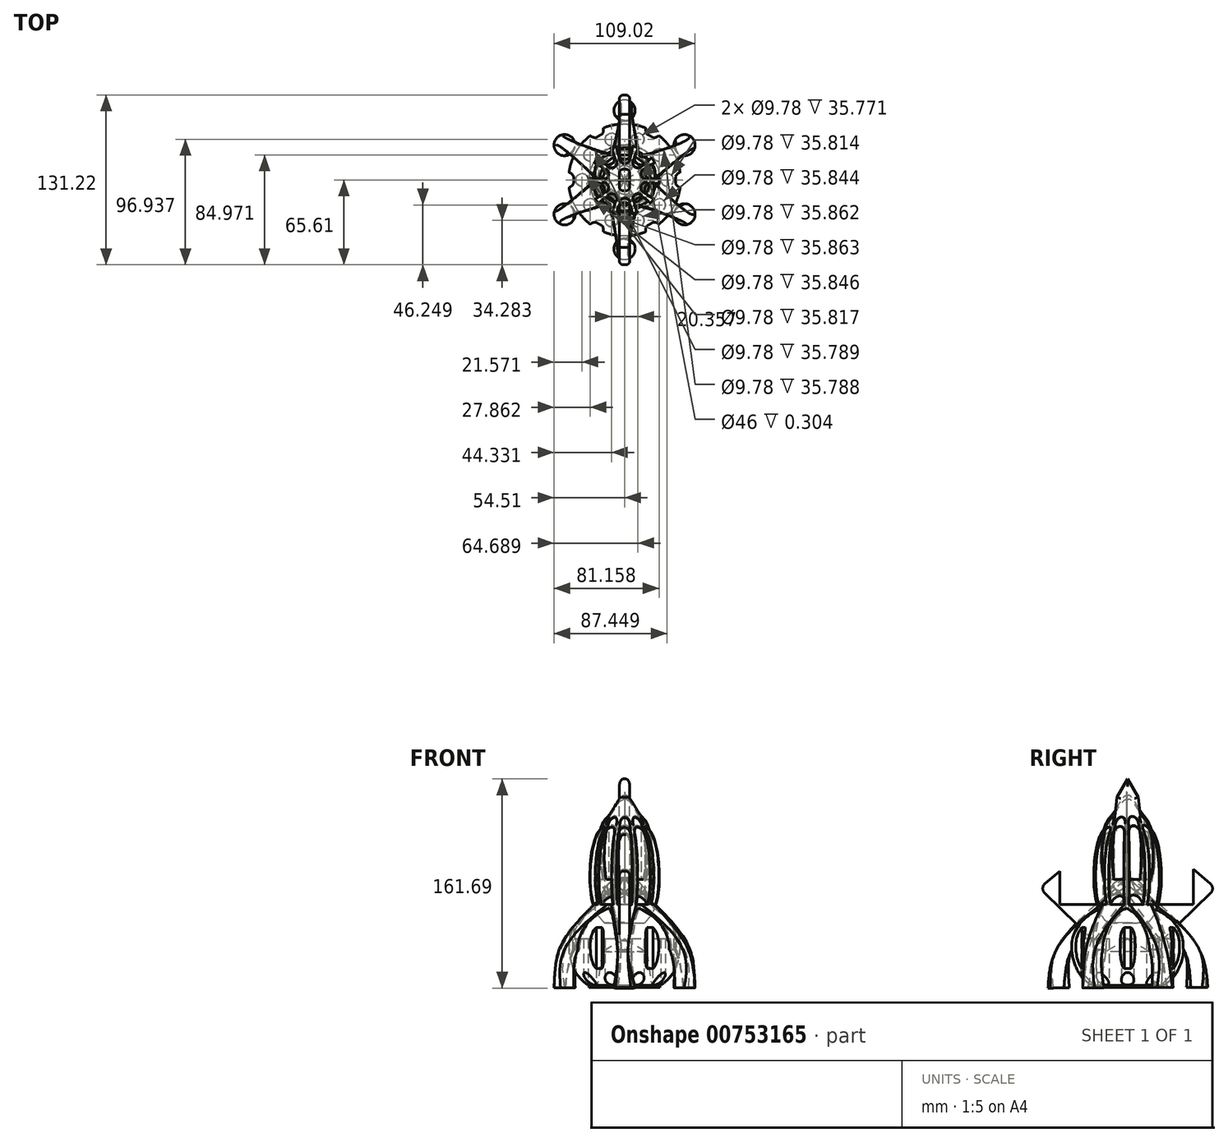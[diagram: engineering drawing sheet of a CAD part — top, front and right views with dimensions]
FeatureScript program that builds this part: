
annotation { "Feature Type Name" : "Feature", "Feature Type Description" : "" }
export const myFeature = defineFeature(function(context is Context, id is Id, definition is map)
    precondition{}
    {
        {
            var Q0;
            Q0=qCreatedBy(makeId("Top.planeOp"),FACE);
            cPlane(context, id + "F0", {"entities" : qUnion([Q0]), "cplaneType" : CPlaneType.OFFSET, "offset" : 28 * mm, "width" : 150 * mm, "height" : 150 * mm});
        }
        {
            var Q0;
            Q0=qCreatedBy(makeId("Top.planeOp"),FACE);
            var sketch = newSketch(context, id + "F1", { "sketchPlane" : qUnion([Q0])});
            skCircle(sketch, "E0", {"center": v(0, -53.65) * mm, "radius": 8.2 * mm});
            skCircle(sketch, "E1.1.0", {"center": v(46.46, -26.82) * mm, "radius": 8.2 * mm});
            skCircle(sketch, "E1.2.0", {"center": v(46.46, 26.82) * mm, "radius": 8.2 * mm});
            skCircle(sketch, "E1.4.0", {"center": v(-46.46, 26.82) * mm, "radius": 8.2 * mm});
            skPoint(sketch, "E1.center", {"position": v(0, 0) * mm});
            skCircle(sketch, "E2.1.5.0", {"center": v(-46.46, -26.82) * mm, "radius": 8.2 * mm});
            skArc(sketch, "E3", {"start": v(7.17, 57.63) * mm, "mid": v(1.7, 61.67) * mm, "end": v(-4.94, 60.2) * mm});
            skArc(sketch, "E4", {"start": v(6.58, 48.75) * mm, "mid": v(8.18, 53.1) * mm, "end": v(7.17, 57.63) * mm});
            skArc(sketch, "E5", {"start": v(-7.1, 49.56) * mm, "mid": v(-0.48, 45.47) * mm, "end": v(6.58, 48.75) * mm});
            skArc(sketch, "E6", {"start": v(-4.94, 60.2) * mm, "mid": v(-8.03, 55.29) * mm, "end": v(-7.1, 49.56) * mm});
            skSolve(sketch);
        }
        {
            var Q0;
            Q0=qCreatedBy(makeId("Right.planeOp"),FACE);
            var sketch = newSketch(context, id + "F2", { "sketchPlane" : qUnion([Q0])});
            skFitSpline(sketch, "E7", {"points": [v(53.84, 0) * mm, v(45.06, 43.34) * mm, v(0, 67.01) * mm], "startDerivative": vector(-1.6, 100.47) * mm, "endDerivative": vector(-104.87, 34.33) * mm});
            skSolve(sketch);
        }
        {
            var Q0;
            Q0=qCreatedBy(id+"F0.planeOp",FACE);
            var sketch = newSketch(context, id + "F3", { "sketchPlane" : qUnion([Q0])});
            skLineSegment(sketch, "E8.bottom", {"start": v(-2.65, 55.9) * mm, "end": v(5.35, 55.9) * mm});
            skLineSegment(sketch, "E8.top", {"start": v(-2.65, 43.9) * mm, "end": v(5.35, 43.9) * mm});
            skLineSegment(sketch, "E8.left", {"start": v(-2.65, 55.9) * mm, "end": v(-2.65, 43.9) * mm});
            skLineSegment(sketch, "E8.right", {"start": v(5.35, 55.9) * mm, "end": v(5.35, 43.9) * mm});
            skLineSegment(sketch, "E9.1.0", {"start": v(-55.65, 13.56) * mm, "end": v(-53.18, 21.17) * mm});
            skLineSegment(sketch, "E9.1.1", {"start": v(-44.24, 9.85) * mm, "end": v(-41.77, 17.46) * mm});
            skLineSegment(sketch, "E9.1.2", {"start": v(-55.65, 13.56) * mm, "end": v(-44.24, 9.85) * mm});
            skLineSegment(sketch, "E9.1.3", {"start": v(-53.18, 21.17) * mm, "end": v(-41.77, 17.46) * mm});
            skLineSegment(sketch, "E9.2.0", {"start": v(-31.77, -49.94) * mm, "end": v(-38.24, -45.23) * mm});
            skLineSegment(sketch, "E9.2.1", {"start": v(-24.71, -40.23) * mm, "end": v(-31.19, -35.53) * mm});
            skLineSegment(sketch, "E9.2.2", {"start": v(-31.77, -49.94) * mm, "end": v(-24.71, -40.23) * mm});
            skLineSegment(sketch, "E9.2.3", {"start": v(-38.24, -45.23) * mm, "end": v(-31.19, -35.53) * mm});
            skLineSegment(sketch, "E9.3.0", {"start": v(36, -46.84) * mm, "end": v(29.53, -51.54) * mm});
            skLineSegment(sketch, "E9.3.1", {"start": v(28.95, -37.13) * mm, "end": v(22.48, -41.83) * mm});
            skLineSegment(sketch, "E9.3.2", {"start": v(36, -46.84) * mm, "end": v(28.95, -37.13) * mm});
            skLineSegment(sketch, "E9.3.3", {"start": v(29.53, -51.54) * mm, "end": v(22.48, -41.83) * mm});
            skLineSegment(sketch, "E9.4.0", {"start": v(54, 18.57) * mm, "end": v(56.47, 10.96) * mm});
            skLineSegment(sketch, "E9.4.1", {"start": v(42.58, 14.86) * mm, "end": v(45.06, 7.25) * mm});
            skLineSegment(sketch, "E9.4.2", {"start": v(54, 18.57) * mm, "end": v(42.58, 14.86) * mm});
            skLineSegment(sketch, "E9.4.3", {"start": v(56.47, 10.96) * mm, "end": v(45.06, 7.25) * mm});
            skPoint(sketch, "E9.center", {"position": v(-0.02, -1.75) * mm});
            skSolve(sketch);
        }
        {
            var Q0;
            Q0=qCreatedBy(makeId("Right.planeOp"),FACE);
            var sketch = newSketch(context, id + "F4", { "sketchPlane" : qUnion([Q0])});
            skLineSegment(sketch, "E10", {"start": v(0.18, 0) * mm, "end": v(-21.05, 0) * mm});
            skFitSpline(sketch, "E11", {"points": [v(-21.05, 0) * mm, v(-42.02, 40.3) * mm, v(-8.37, 66.57) * mm, v(-0.13, 65.47) * mm], "startDerivative": vector(-109.76, 0) * mm, "endDerivative": vector(42.44, -18.45) * mm});
            skLineSegment(sketch, "E12", {"start": v(-0.13, 65.47) * mm, "end": v(0.18, 0) * mm});
            skLineSegment(sketch, "E13", {"start": v(-21.05, 0) * mm, "end": v(-17.07, 27.44) * mm});
            skLineSegment(sketch, "E14", {"start": v(-17.07, 27.44) * mm, "end": v(0, 37.41) * mm});
            skSolve(sketch);
        }
        {
            var Q0;
            {var subQ0=sQuery(id+"F4.wireOp",EDGE,"E11");Q0=makeQuery(id+"F4.imprint","IMPRINT",FACE,{"disambiguationData":[TD([[makeQuery(id+"F4.imprint","IMPRINT",EDGE,{"derivedFrom":subQ0}),-1.0]])]});}
            var Q1;
            Q1=sQuery(id+"F4.wireOp",EDGE,"E12");
            revolve(context, id + "F5", {"surfaceOperationType" : NewSurfaceOperationType.NEW, "entities" : qUnion([Q0]), "axis" : qUnion([Q1]), "revolveType" : RevolveType.FULL});
        }
        {
            var Q0;
            Q0=qCreatedBy(id+"F0.planeOp",FACE);
            cPlane(context, id + "F6", {"entities" : qUnion([Q0]), "cplaneType" : CPlaneType.OFFSET, "offset" : 36 * mm, "width" : 150 * mm, "height" : 150 * mm});
        }
        {
            var Q0;
            Q0=qCreatedBy(makeId("Front.planeOp"),FACE);
            var sketch = newSketch(context, id + "F7", { "sketchPlane" : qUnion([Q0])});
            skArc(sketch, "E15", {"start": v(-13.56, 78.8) * mm, "mid": v(-18.17, 66.48) * mm, "end": v(-13.26, 54.27) * mm});
            skArc(sketch, "E16", {"start": v(-13.26, 54.27) * mm, "mid": v(2.4, 48.69) * mm, "end": v(16.05, 58.17) * mm});
            skArc(sketch, "E17", {"start": v(16.05, 58.17) * mm, "mid": v(18.07, 68.66) * mm, "end": v(13.85, 78.48) * mm});
            skArc(sketch, "E18", {"start": v(13.85, 78.48) * mm, "mid": v(0.22, 84.88) * mm, "end": v(-13.56, 78.8) * mm});
            skSolve(sketch);
        }
        {
            var Q1;
            Q1=makeQuery(id+"F1.imprint","IMPRINT",FACE,{"disambiguationData":[TD([[makeQuery(id+"F1.imprint","IMPRINT",EDGE,{"derivedFrom":sQuery(id+"F1.wireOp",EDGE,"E3")}),1.0]])]});
            var Q2;
            Q2=makeQuery(id+"F3.imprint","IMPRINT",FACE,{"disambiguationData":[TD([[makeQuery(id+"F3.imprint","IMPRINT",EDGE,{"derivedFrom":sQuery(id+"F3.wireOp",EDGE,"E8.bottom")}),-1.0]])]});
            var Q3;
            Q3=makeQuery(id+"F7.imprint","IMPRINT",FACE,{"disambiguationData":[TD([[makeQuery(id+"F7.imprint","IMPRINT",EDGE,{"derivedFrom":sQuery(id+"F7.wireOp",EDGE,"E15")}),1.0]])]});
            var Q4;
            Q4=sQuery(id+"F2.wireOp",EDGE,"E7");
            loft(context, id + "F8", {"sheetProfilesArray" : [{ "sheetProfileEntities" : qUnion([Q1]) }, { "sheetProfileEntities" : qUnion([Q2]) }, { "sheetProfileEntities" : qUnion([Q3]) }], "guidesArray" : [{ "guideEntities" : qUnion([Q4]), "guideDerivativeType" : LoftGuideDerivativeType.DEFAULT, "guideDerivativeMagnitude" : 1 }]});
        }
        {
            var Q0;
            Q0=makeQuery(id+"F8.opLoft","SWEPT_BODY",BODY,{"disambiguationData":[OSD([makeQuery(id+"F1.imprint","IMPRINT",FACE,{"disambiguationData":[TD([[makeQuery(id+"F1.imprint","IMPRINT",EDGE,{"derivedFrom":sQuery(id+"F1.wireOp",EDGE,"E3")}),1.0]])]}),sQuery(id+"F3.wireOp",EDGE,"E8.left"),makeQuery(id+"F7.imprint","IMPRINT",FACE,{"disambiguationData":[TD([[makeQuery(id+"F7.imprint","IMPRINT",EDGE,{"derivedFrom":sQuery(id+"F7.wireOp",EDGE,"E15")}),1.0]])]})])]});
            var Q1;
            Q1=sQuery(id+"F4.wireOp",EDGE,"E12");
            circularPattern(context, id + "F9", {"operationType" : NewBodyOperationType.ADD, "entities" : qUnion([Q0]), "axis" : qUnion([Q1]), "angle" : 360 * degree, "instanceCount" : 6, "equalSpace" : true, "isCentered" : true});
        }
        {
            var Q0;
            Q0=qCreatedBy(makeId("Front.planeOp"),FACE);
            var sketch = newSketch(context, id + "F10", { "sketchPlane" : qUnion([Q0])});
            skFitSpline(sketch, "E19", {"points": [v(-15.35, 49.67) * mm, v(-24.47, 64.82) * mm, v(-25.38, 104.6) * mm, v(-19.75, 121) * mm, v(-12.6, 129.8) * mm, v(0, 145.27) * mm, v(10.93, 128.5) * mm], "startDerivative": vector(-59.94, 59.18) * mm, "endDerivative": vector(86, -27.64) * mm});
            skLineSegment(sketch, "E20", {"start": v(0, 50.04) * mm, "end": v(-15.35, 49.67) * mm});
            skLineSegment(sketch, "E21", {"start": v(0, 50.04) * mm, "end": v(0, 145.27) * mm});
            skSolve(sketch);
        }
        {
            var Q0;
            {var subQ0=sQuery(id+"F10.wireOp",EDGE,"E20");Q0=makeQuery(id+"F10.imprint","IMPRINT",FACE,{"disambiguationData":[TD([[makeQuery(id+"F10.imprint","IMPRINT",EDGE,{"derivedFrom":subQ0}),-1.0]])]});}
            var Q1;
            Q1=sQuery(id+"F10.wireOp",EDGE,"E21");
            revolve(context, id + "F11", {"surfaceOperationType" : NewSurfaceOperationType.NEW, "entities" : qUnion([Q0]), "axis" : qUnion([Q1]), "revolveType" : RevolveType.FULL});
        }
        {
            var Q0;
            {var subQ0=sQuery(id+"F10.wireOp",EDGE,"E20");Q0=makeQuery(id+"F10.imprint","IMPRINT",FACE,{"disambiguationData":[TD([[makeQuery(id+"F10.imprint","IMPRINT",EDGE,{"derivedFrom":subQ0}),-1.0]])]});}
            var Q1;
            Q1=sQuery(id+"F10.wireOp",EDGE,"E21");
            revolve(context, id + "F12", {"surfaceOperationType" : NewSurfaceOperationType.NEW, "entities" : qUnion([Q0]), "axis" : qUnion([Q1]), "revolveType" : RevolveType.FULL});
        }
        {
            var Q0;
            Q0=qCreatedBy(makeId("Right.planeOp"),FACE);
            var sketch = newSketch(context, id + "F13", { "sketchPlane" : qUnion([Q0])});
            skLineSegment(sketch, "E22", {"start": v(26.03, 35.86) * mm, "end": v(64.1, 72.83) * mm});
            skLineSegment(sketch, "E23", {"start": v(63.8, 80.26) * mm, "end": v(22.57, 114.6) * mm});
            skLineSegment(sketch, "E24", {"start": v(22.57, 114.6) * mm, "end": v(11.06, 122.62) * mm});
            skLineSegment(sketch, "E25", {"start": v(11.06, 122.62) * mm, "end": v(8.34, 146.93) * mm});
            skLineSegment(sketch, "E26", {"start": v(8.34, 146.93) * mm, "end": v(0, 161.11) * mm});
            skLineSegment(sketch, "E27", {"start": v(0, 161.11) * mm, "end": v(0, 10.58) * mm});
            skLineSegment(sketch, "E28.MirrorCS", {"start": v(-8.34, 146.93) * mm, "end": v(0, 161.11) * mm});
            skLineSegment(sketch, "E29.MirrorCS", {"start": v(-11.06, 122.62) * mm, "end": v(-8.34, 146.93) * mm});
            skLineSegment(sketch, "E30.MirrorCS", {"start": v(-63.8, 80.26) * mm, "end": v(-22.57, 114.6) * mm});
            skLineSegment(sketch, "E31.MirrorCS", {"start": v(-26.03, 35.86) * mm, "end": v(-64.1, 72.83) * mm});
            skLineSegment(sketch, "E32.MirrorCS", {"start": v(-22.57, 114.6) * mm, "end": v(-11.06, 122.62) * mm});
            skPoint(sketch, "E33", {"position": v(47.66, 93.7) * mm});
            skPoint(sketch, "E34.visualSharp", {"position": v(68.08, 76.7) * mm});
            skArc(sketch, "E34.filletArc", {"start": v(64.1, 72.83) * mm, "mid": v(65.6, 76.6) * mm, "end": v(63.8, 80.26) * mm});
            skPoint(sketch, "E35.visualSharp", {"position": v(-68.08, 76.7) * mm});
            skArc(sketch, "E35.filletArc", {"start": v(-63.8, 80.26) * mm, "mid": v(-65.6, 76.6) * mm, "end": v(-64.1, 72.83) * mm});
            skLineSegment(sketch, "E36", {"start": v(26.03, 35.86) * mm, "end": v(0, 72.2) * mm});
            skLineSegment(sketch, "E37.MirrorCS", {"start": v(-26.03, 35.86) * mm, "end": v(0, 72.2) * mm});
            skPoint(sketch, "E38.orphan", {"position": v(0, 10.58) * mm});
            skSolve(sketch);
        }
        {
            var Q0;
            Q0=qSketchRegion(id+"F13",true);
            extrude(context, id + "F14", {"entities" : qUnion([Q0]), "endBound" : BoundingType.SYMMETRIC, "depth" : 8 * mm, "offsetDistance" : 25 * mm});
        }
        {
            var Q0;
            Q0=makeQuery(id+"F14.opExtrude","CAP_FACE",FACE,{"disambiguationData":[OSD([sQuery(id+"F13.wireOp",EDGE,"E22"),sQuery(id+"F13.wireOp",EDGE,"E23"),sQuery(id+"F13.wireOp",EDGE,"E24"),sQuery(id+"F13.wireOp",EDGE,"E25"),sQuery(id+"F13.wireOp",EDGE,"E26"),sQuery(id+"F13.wireOp",EDGE,"E28.MirrorCS"),sQuery(id+"F13.wireOp",EDGE,"E29.MirrorCS"),sQuery(id+"F13.wireOp",EDGE,"E30.MirrorCS"),sQuery(id+"F13.wireOp",EDGE,"E31.MirrorCS"),sQuery(id+"F13.wireOp",EDGE,"E32.MirrorCS")])],"isStart":true});
            var Q1;
            Q1=makeQuery(id+"F14.opExtrude","CAP_FACE",FACE,{"disambiguationData":[OSD([sQuery(id+"F13.wireOp",EDGE,"E22"),sQuery(id+"F13.wireOp",EDGE,"E23"),sQuery(id+"F13.wireOp",EDGE,"E24"),sQuery(id+"F13.wireOp",EDGE,"E25"),sQuery(id+"F13.wireOp",EDGE,"E26"),sQuery(id+"F13.wireOp",EDGE,"E28.MirrorCS"),sQuery(id+"F13.wireOp",EDGE,"E29.MirrorCS"),sQuery(id+"F13.wireOp",EDGE,"E30.MirrorCS"),sQuery(id+"F13.wireOp",EDGE,"E31.MirrorCS"),sQuery(id+"F13.wireOp",EDGE,"E32.MirrorCS")])],"isStart":false});
            fillet(context, id + "F15", {"entities" : qUnion([Q0, Q1]), "radius" : 3 * mm, "tangentPropagation" : true, "allowEdgeOverflow" : false});
        }
        {
            var Q0;
            Q0=qCreatedBy(makeId("Top.planeOp"),FACE);
            var sketch = newSketch(context, id + "F16", { "sketchPlane" : qUnion([Q0])});
            skCircle(sketch, "E39", {"center": v(32.94, 0) * mm, "radius": 4.89 * mm});
            skCircle(sketch, "E40.1.0", {"center": v(26.65, 19.36) * mm, "radius": 4.89 * mm});
            skCircle(sketch, "E40.2.0", {"center": v(10.18, 31.33) * mm, "radius": 4.89 * mm});
            skCircle(sketch, "E40.3.0", {"center": v(-10.18, 31.33) * mm, "radius": 4.89 * mm});
            skCircle(sketch, "E40.4.0", {"center": v(-26.65, 19.36) * mm, "radius": 4.89 * mm});
            skPoint(sketch, "E40.center", {"position": v(0, 0) * mm});
            skCircle(sketch, "E41.1.5.0", {"center": v(-32.94, 0) * mm, "radius": 4.89 * mm});
            skCircle(sketch, "E41.1.6.0", {"center": v(-26.65, -19.36) * mm, "radius": 4.89 * mm});
            skCircle(sketch, "E41.1.7.0", {"center": v(-10.18, -31.33) * mm, "radius": 4.89 * mm});
            skCircle(sketch, "E41.1.8.0", {"center": v(10.18, -31.33) * mm, "radius": 4.89 * mm});
            skCircle(sketch, "E41.1.9.0", {"center": v(26.65, -19.36) * mm, "radius": 4.89 * mm});
            skSolve(sketch);
        }
        {
            var Q0;
            Q0=qSketchRegion(id+"F16",true);
            extrude(context, id + "F17", {"entities" : qUnion([Q0]), "operationType" : NewBodyOperationType.REMOVE, "depth" : 37.6 * mm, "offsetDistance" : 25 * mm});
        }
        {
            var Q0;
            Q0=qCreatedBy(id+"F6.planeOp",FACE);
            var sketch = newSketch(context, id + "F18", { "sketchPlane" : qUnion([Q0])});
            skLineSegment(sketch, "E42", {"start": v(4.87, -21.36) * mm, "end": v(11.93, -52.3) * mm});
            skLineSegment(sketch, "E43", {"start": v(11.93, -52.3) * mm, "end": v(0, -52.3) * mm});
            skLineSegment(sketch, "E44", {"start": v(0, -52.3) * mm, "end": v(0, 0) * mm});
            skLineSegment(sketch, "E45.MirrorCS", {"start": v(-4.87, -21.36) * mm, "end": v(-11.93, -52.3) * mm});
            skLineSegment(sketch, "E46.MirrorCS", {"start": v(-11.93, -52.3) * mm, "end": v(0, -52.3) * mm});
            skPoint(sketch, "E47.visualSharp", {"position": v(0, 0) * mm});
            skArc(sketch, "E47.filletArc", {"start": v(4.87, -21.36) * mm, "mid": v(0, -17.47) * mm, "end": v(-4.87, -21.36) * mm});
            skLineSegment(sketch, "E48.1.0", {"start": v(39.9, -35.44) * mm, "end": v(30.25, -42.46) * mm});
            skPoint(sketch, "E48.1.1", {"position": v(-0.48, -0.15) * mm});
            skLineSegment(sketch, "E48.1.2", {"start": v(16.01, -14.57) * mm, "end": v(39.9, -35.44) * mm});
            skArc(sketch, "E48.1.3", {"start": v(16.01, -14.57) * mm, "mid": v(9.79, -14.29) * mm, "end": v(8.13, -20.3) * mm});
            skLineSegment(sketch, "E48.1.4", {"start": v(8.13, -20.3) * mm, "end": v(20.6, -49.47) * mm});
            skLineSegment(sketch, "E48.1.5", {"start": v(20.6, -49.47) * mm, "end": v(30.25, -42.46) * mm});
            skLineSegment(sketch, "E48.1.6", {"start": v(30.25, -42.46) * mm, "end": v(-0.48, -0.15) * mm});
            skLineSegment(sketch, "E48.2.0", {"start": v(52.63, -5.37) * mm, "end": v(48.95, -16.72) * mm});
            skPoint(sketch, "E48.2.1", {"position": v(-0.79, -0.56) * mm});
            skLineSegment(sketch, "E48.2.2", {"start": v(21.03, -2.52) * mm, "end": v(52.63, -5.37) * mm});
            skArc(sketch, "E48.2.3", {"start": v(21.03, -2.52) * mm, "mid": v(15.83, -5.96) * mm, "end": v(18.02, -11.8) * mm});
            skLineSegment(sketch, "E48.2.4", {"start": v(18.02, -11.8) * mm, "end": v(45.26, -28.07) * mm});
            skLineSegment(sketch, "E48.2.5", {"start": v(45.26, -28.07) * mm, "end": v(48.95, -16.72) * mm});
            skLineSegment(sketch, "E48.2.6", {"start": v(48.95, -16.72) * mm, "end": v(-0.79, -0.56) * mm});
            skLineSegment(sketch, "E48.3.0", {"start": v(45.25, 26.44) * mm, "end": v(48.94, 15.1) * mm});
            skPoint(sketch, "E48.3.1", {"position": v(-0.8, -1.07) * mm});
            skLineSegment(sketch, "E48.3.2", {"start": v(18.02, 10.17) * mm, "end": v(45.25, 26.44) * mm});
            skArc(sketch, "E48.3.3", {"start": v(18.02, 10.17) * mm, "mid": v(15.83, 4.33) * mm, "end": v(21.03, 0.9) * mm});
            skLineSegment(sketch, "E48.3.4", {"start": v(21.03, 0.9) * mm, "end": v(52.63, 3.74) * mm});
            skLineSegment(sketch, "E48.3.5", {"start": v(52.63, 3.74) * mm, "end": v(48.94, 15.1) * mm});
            skLineSegment(sketch, "E48.3.6", {"start": v(48.94, 15.1) * mm, "end": v(-0.8, -1.07) * mm});
            skLineSegment(sketch, "E48.4.0", {"start": v(20.59, 47.84) * mm, "end": v(30.24, 40.82) * mm});
            skPoint(sketch, "E48.4.1", {"position": v(-0.5, -1.48) * mm});
            skLineSegment(sketch, "E48.4.2", {"start": v(8.12, 18.66) * mm, "end": v(20.59, 47.84) * mm});
            skArc(sketch, "E48.4.3", {"start": v(8.12, 18.66) * mm, "mid": v(9.77, 12.65) * mm, "end": v(16, 12.93) * mm});
            skLineSegment(sketch, "E48.4.4", {"start": v(16, 12.93) * mm, "end": v(39.9, 33.8) * mm});
            skLineSegment(sketch, "E48.4.5", {"start": v(39.9, 33.8) * mm, "end": v(30.24, 40.82) * mm});
            skLineSegment(sketch, "E48.4.6", {"start": v(30.24, 40.82) * mm, "end": v(-0.5, -1.48) * mm});
            skLineSegment(sketch, "E48.5.0", {"start": v(-11.95, 50.65) * mm, "end": v(-0.01, 50.65) * mm});
            skPoint(sketch, "E48.5.1", {"position": v(-0.01, -1.64) * mm});
            skLineSegment(sketch, "E48.5.2", {"start": v(-4.89, 19.72) * mm, "end": v(-11.95, 50.65) * mm});
            skArc(sketch, "E48.5.3", {"start": v(-4.89, 19.72) * mm, "mid": v(-0.01, 15.83) * mm, "end": v(4.86, 19.72) * mm});
            skLineSegment(sketch, "E48.5.4", {"start": v(4.86, 19.72) * mm, "end": v(11.92, 50.65) * mm});
            skLineSegment(sketch, "E48.5.5", {"start": v(11.92, 50.65) * mm, "end": v(-0.01, 50.65) * mm});
            skLineSegment(sketch, "E48.5.6", {"start": v(-0.01, 50.65) * mm, "end": v(-0.01, -1.64) * mm});
            skLineSegment(sketch, "E48.6.0", {"start": v(-39.92, 33.8) * mm, "end": v(-30.27, 40.82) * mm});
            skPoint(sketch, "E48.6.1", {"position": v(0.47, -1.49) * mm});
            skLineSegment(sketch, "E48.6.2", {"start": v(-16.03, 12.93) * mm, "end": v(-39.92, 33.8) * mm});
            skArc(sketch, "E48.6.3", {"start": v(-16.03, 12.93) * mm, "mid": v(-9.8, 12.65) * mm, "end": v(-8.14, 18.66) * mm});
            skLineSegment(sketch, "E48.6.4", {"start": v(-8.14, 18.66) * mm, "end": v(-20.61, 47.83) * mm});
            skLineSegment(sketch, "E48.6.5", {"start": v(-20.61, 47.83) * mm, "end": v(-30.27, 40.82) * mm});
            skLineSegment(sketch, "E48.6.6", {"start": v(-30.27, 40.82) * mm, "end": v(0.47, -1.49) * mm});
            skLineSegment(sketch, "E48.7.0", {"start": v(-52.65, 3.73) * mm, "end": v(-48.96, 15.08) * mm});
            skPoint(sketch, "E48.7.1", {"position": v(0.77, -1.08) * mm});
            skLineSegment(sketch, "E48.7.2", {"start": v(-21.05, 0.88) * mm, "end": v(-52.65, 3.73) * mm});
            skArc(sketch, "E48.7.3", {"start": v(-21.05, 0.88) * mm, "mid": v(-15.85, 4.32) * mm, "end": v(-18.04, 10.16) * mm});
            skLineSegment(sketch, "E48.7.4", {"start": v(-18.04, 10.16) * mm, "end": v(-45.27, 26.43) * mm});
            skLineSegment(sketch, "E48.7.5", {"start": v(-45.27, 26.43) * mm, "end": v(-48.96, 15.08) * mm});
            skLineSegment(sketch, "E48.7.6", {"start": v(-48.96, 15.08) * mm, "end": v(0.77, -1.08) * mm});
            skLineSegment(sketch, "E48.8.0", {"start": v(-45.27, -28.08) * mm, "end": v(-48.96, -16.73) * mm});
            skPoint(sketch, "E48.8.1", {"position": v(0.78, -0.57) * mm});
            skLineSegment(sketch, "E48.8.2", {"start": v(-18.03, -11.81) * mm, "end": v(-45.27, -28.08) * mm});
            skArc(sketch, "E48.8.3", {"start": v(-18.03, -11.81) * mm, "mid": v(-15.84, -5.97) * mm, "end": v(-21.04, -2.54) * mm});
            skLineSegment(sketch, "E48.8.4", {"start": v(-21.04, -2.54) * mm, "end": v(-52.64, -5.38) * mm});
            skLineSegment(sketch, "E48.8.5", {"start": v(-52.64, -5.38) * mm, "end": v(-48.96, -16.73) * mm});
            skLineSegment(sketch, "E48.8.6", {"start": v(-48.96, -16.73) * mm, "end": v(0.78, -0.57) * mm});
            skLineSegment(sketch, "E48.9.0", {"start": v(-20.6, -49.48) * mm, "end": v(-30.25, -42.46) * mm});
            skPoint(sketch, "E48.9.1", {"position": v(0.48, -0.16) * mm});
            skLineSegment(sketch, "E48.9.2", {"start": v(-8.13, -20.3) * mm, "end": v(-20.6, -49.48) * mm});
            skArc(sketch, "E48.9.3", {"start": v(-8.13, -20.3) * mm, "mid": v(-9.79, -14.3) * mm, "end": v(-16.02, -14.58) * mm});
            skLineSegment(sketch, "E48.9.4", {"start": v(-16.02, -14.58) * mm, "end": v(-39.9, -35.45) * mm});
            skLineSegment(sketch, "E48.9.5", {"start": v(-39.9, -35.45) * mm, "end": v(-30.25, -42.46) * mm});
            skLineSegment(sketch, "E48.9.6", {"start": v(-30.25, -42.46) * mm, "end": v(0.48, -0.16) * mm});
            skPoint(sketch, "E48.center", {"position": v(0, -0.82) * mm});
            skSolve(sketch);
        }
        {
            var Q0;
            Q0=qCreatedBy(makeId("Top.planeOp"),FACE);
            var sketch = newSketch(context, id + "F19", { "sketchPlane" : qUnion([Q0])});
            skCircle(sketch, "E49", {"center": v(0, 0) * mm, "radius": 39.4 * mm});
            skCircle(sketch, "E50", {"center": v(-44.9, 0) * mm, "radius": 6.17 * mm});
            skCircle(sketch, "E51.1.0", {"center": v(-22.45, -38.88) * mm, "radius": 6.17 * mm});
            skCircle(sketch, "E51.2.0", {"center": v(22.45, -38.88) * mm, "radius": 6.17 * mm});
            skCircle(sketch, "E51.3.0", {"center": v(44.9, 0) * mm, "radius": 6.17 * mm});
            skCircle(sketch, "E51.4.0", {"center": v(22.45, 38.88) * mm, "radius": 6.17 * mm});
            skCircle(sketch, "E51.5.0", {"center": v(-22.45, 38.88) * mm, "radius": 6.17 * mm});
            skSolve(sketch);
        }
        {
            var Q0;
            {var subQ0=sQuery(id+"F19.wireOp",EDGE,"E51.1.0");var subQ1=sQuery(id+"F19.wireOp",EDGE,"E49");var subQ2=makeQuery(id+"F19.imprint","INTERSECT",VERTEX,{"disambiguationData":[OD(0.0)],"derivedFrom":[subQ1,subQ0]});Q0=makeQuery(id+"F19.imprint","IMPRINT",FACE,{"disambiguationData":[TD([[makeQuery(id+"F19.imprint","IMPRINT",EDGE,{"disambiguationData":[TD([[subQ2,-1.0]])],"derivedFrom":subQ1}),-1.0]])]});}
            var Q1;
            {var subQ0=sQuery(id+"F19.wireOp",EDGE,"E51.2.0");var subQ1=sQuery(id+"F19.wireOp",EDGE,"E49");var subQ2=makeQuery(id+"F19.imprint","INTERSECT",VERTEX,{"disambiguationData":[OD(0.0)],"derivedFrom":[subQ1,subQ0]});Q1=makeQuery(id+"F19.imprint","IMPRINT",FACE,{"disambiguationData":[TD([[makeQuery(id+"F19.imprint","IMPRINT",EDGE,{"disambiguationData":[TD([[subQ2,-1.0]])],"derivedFrom":subQ1}),-1.0]])]});}
            var Q2;
            {var subQ0=sQuery(id+"F19.wireOp",EDGE,"E51.3.0");var subQ1=sQuery(id+"F19.wireOp",EDGE,"E49");var subQ2=makeQuery(id+"F19.imprint","INTERSECT",VERTEX,{"disambiguationData":[OD(0.0)],"derivedFrom":[subQ1,subQ0]});Q2=makeQuery(id+"F19.imprint","IMPRINT",FACE,{"disambiguationData":[TD([[makeQuery(id+"F19.imprint","IMPRINT",EDGE,{"disambiguationData":[TD([[subQ2,1.0]])],"derivedFrom":subQ1}),-1.0]])]});}
            var Q3;
            {var subQ0=sQuery(id+"F19.wireOp",EDGE,"E51.4.0");var subQ1=sQuery(id+"F19.wireOp",EDGE,"E49");var subQ2=makeQuery(id+"F19.imprint","INTERSECT",VERTEX,{"disambiguationData":[OD(0.0)],"derivedFrom":[subQ1,subQ0]});Q3=makeQuery(id+"F19.imprint","IMPRINT",FACE,{"disambiguationData":[TD([[makeQuery(id+"F19.imprint","IMPRINT",EDGE,{"disambiguationData":[TD([[subQ2,-1.0]])],"derivedFrom":subQ1}),-1.0]])]});}
            var Q4;
            {var subQ0=sQuery(id+"F19.wireOp",EDGE,"E51.5.0");var subQ1=sQuery(id+"F19.wireOp",EDGE,"E49");var subQ2=makeQuery(id+"F19.imprint","INTERSECT",VERTEX,{"disambiguationData":[OD(0.0)],"derivedFrom":[subQ1,subQ0]});Q4=makeQuery(id+"F19.imprint","IMPRINT",FACE,{"disambiguationData":[TD([[makeQuery(id+"F19.imprint","IMPRINT",EDGE,{"disambiguationData":[TD([[subQ2,-1.0]])],"derivedFrom":subQ1}),-1.0]])]});}
            var Q5;
            {var subQ0=sQuery(id+"F19.wireOp",EDGE,"E50");var subQ1=sQuery(id+"F19.wireOp",EDGE,"E49");var subQ2=makeQuery(id+"F19.imprint","INTERSECT",VERTEX,{"disambiguationData":[OD(0.0)],"derivedFrom":[subQ1,subQ0]});Q5=makeQuery(id+"F19.imprint","IMPRINT",FACE,{"disambiguationData":[TD([[makeQuery(id+"F19.imprint","IMPRINT",EDGE,{"disambiguationData":[TD([[subQ2,-1.0]])],"derivedFrom":subQ1}),-1.0]])]});}
            extrude(context, id + "F20", {"entities" : qUnion([Q0, Q1, Q2, Q3, Q4, Q5]), "operationType" : NewBodyOperationType.REMOVE, "depth" : 123.3 * mm, "offsetDistance" : 25 * mm});
        }
        {
            var Q0;
            Q0=qSketchRegion(id+"F18",true);
            extrude(context, id + "F21", {"entities" : qUnion([Q0]), "operationType" : NewBodyOperationType.REMOVE, "depth" : 87 * mm, "offsetDistance" : 25 * mm});
        }
        {
            var Q0;
            Q0=makeQuery(id+"F21.boolean.opBoolean","COPY",FACE,{"derivedFrom":makeQuery(id+"F21.opExtrude","SWEPT_FACE",FACE,{"disambiguationData":[OSD([sQuery(id+"F18.wireOp",EDGE,"E48.4.3")])]})});
            var Q1;
            Q1=makeQuery(id+"F21.boolean.opBoolean","COPY",FACE,{"derivedFrom":makeQuery(id+"F21.opExtrude","SWEPT_FACE",FACE,{"disambiguationData":[OSD([sQuery(id+"F18.wireOp",EDGE,"E48.5.3")])]})});
            var Q2;
            Q2=makeQuery(id+"F21.boolean.opBoolean","COPY",FACE,{"derivedFrom":makeQuery(id+"F21.opExtrude","SWEPT_FACE",FACE,{"disambiguationData":[OSD([sQuery(id+"F18.wireOp",EDGE,"E48.6.3")])]})});
            var Q3;
            Q3=makeQuery(id+"F21.boolean.opBoolean","COPY",FACE,{"derivedFrom":makeQuery(id+"F21.opExtrude","SWEPT_FACE",FACE,{"disambiguationData":[OSD([sQuery(id+"F18.wireOp",EDGE,"E48.3.3")])]})});
            var Q4;
            Q4=makeQuery(id+"F21.boolean.opBoolean","COPY",FACE,{"derivedFrom":makeQuery(id+"F21.opExtrude","SWEPT_FACE",FACE,{"disambiguationData":[OSD([sQuery(id+"F18.wireOp",EDGE,"E48.2.3")])]})});
            var Q5;
            Q5=makeQuery(id+"F21.boolean.opBoolean","COPY",FACE,{"derivedFrom":makeQuery(id+"F21.opExtrude","SWEPT_FACE",FACE,{"disambiguationData":[OSD([sQuery(id+"F18.wireOp",EDGE,"E48.1.3")])]})});
            var Q6;
            Q6=makeQuery(id+"F21.boolean.opBoolean","COPY",FACE,{"derivedFrom":makeQuery(id+"F21.opExtrude","SWEPT_FACE",FACE,{"disambiguationData":[OSD([sQuery(id+"F18.wireOp",EDGE,"E47.filletArc")])]})});
            var Q7;
            Q7=makeQuery(id+"F21.boolean.opBoolean","COPY",FACE,{"derivedFrom":makeQuery(id+"F21.opExtrude","SWEPT_FACE",FACE,{"disambiguationData":[OSD([sQuery(id+"F18.wireOp",EDGE,"E48.9.3")])]})});
            var Q8;
            Q8=makeQuery(id+"F21.boolean.opBoolean","COPY",FACE,{"derivedFrom":makeQuery(id+"F21.opExtrude","SWEPT_FACE",FACE,{"disambiguationData":[OSD([sQuery(id+"F18.wireOp",EDGE,"E48.8.3")])]})});
            var Q9;
            Q9=makeQuery(id+"F21.boolean.opBoolean","COPY",FACE,{"derivedFrom":makeQuery(id+"F21.opExtrude","SWEPT_FACE",FACE,{"disambiguationData":[OSD([sQuery(id+"F18.wireOp",EDGE,"E48.7.3")])]})});
            fillet(context, id + "F22", {"entities" : qUnion([Q0, Q1, Q2, Q3, Q4, Q5, Q6, Q7, Q8, Q9]), "radius" : 0.2 * mm, "tangentPropagation" : true, "allowEdgeOverflow" : false});
        }
        {
            var Q0;
            Q0=qCreatedBy(makeId("Top.planeOp"),FACE);
            var sketch = newSketch(context, id + "F23", { "sketchPlane" : qUnion([Q0])});
            skCircle(sketch, "E52", {"center": v(0, 0) * mm, "radius": 23 * mm});
            skCircle(sketch, "E53", {"center": v(0, 0) * mm, "radius": 27.37 * mm});
            skSolve(sketch);
        }
        {
            var Q0;
            Q0=qSketchRegion(id+"F23",true);
            extrude(context, id + "F24", {"entities" : qUnion([Q0]), "operationType" : NewBodyOperationType.ADD, "depth" : 3 * mm, "offsetDistance" : 25 * mm});
        }
        {
            var Q0;
            Q0=makeQuery(id+"F12.opRevolve","SWEPT_BODY",BODY,{"disambiguationData":[OSD([sQuery(id+"F10.wireOp",EDGE,"E19"),sQuery(id+"F10.wireOp",EDGE,"E20"),sQuery(id+"F10.wireOp",EDGE,"E21")])]});
            var Q1;
            {var subQ0=sQuery(id+"F13.wireOp",EDGE,"E28.MirrorCS");var subQ1=sQuery(id+"F13.wireOp",EDGE,"E26");Q1=makeQuery(id+"F15.opFillet","BLEND_VERTEX",VERTEX,{"blendedFrom":[makeQuery(id+"F14.opExtrude","CAP_EDGE",EDGE,{"disambiguationData":[OSD([subQ1])],"isStart":false}),makeQuery(id+"F14.opExtrude","CAP_EDGE",EDGE,{"disambiguationData":[OSD([subQ0])],"isStart":false}),makeQuery(id+"F14.opExtrude","SWEPT_FACE",FACE,{"disambiguationData":[OSD([subQ1])]}),makeQuery(id+"F14.opExtrude","SWEPT_FACE",FACE,{"disambiguationData":[OSD([subQ0])]})],"blendedInto":[makeQuery(id+"F14.opExtrude","SWEPT_FACE",FACE,{"disambiguationData":[OSD([subQ1])]}),makeQuery(id+"F14.opExtrude","SWEPT_FACE",FACE,{"disambiguationData":[OSD([subQ0])]})]});}
            transform(context, id + "F25", {"entities" : qUnion([Q0]), "transformType" : TransformType.SCALE_UNIFORMLY, "scale" : 0.8, "scalePoint" : qUnion([Q1]), "makeCopy" : false});
        }
    });
